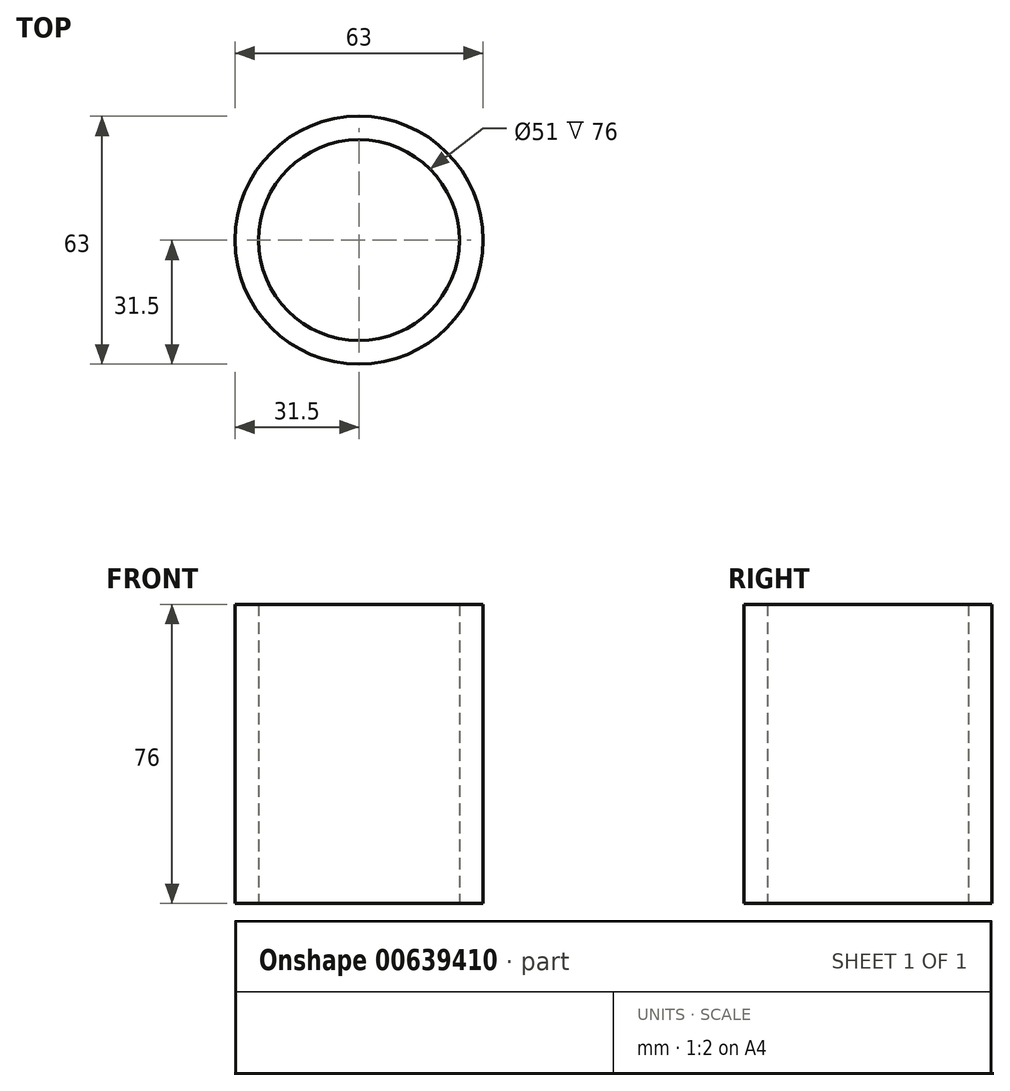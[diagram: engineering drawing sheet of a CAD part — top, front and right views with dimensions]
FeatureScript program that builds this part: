
annotation { "Feature Type Name" : "Feature", "Feature Type Description" : "" }
export const myFeature = defineFeature(function(context is Context, id is Id, definition is map)
    precondition{}
    {
        {
            var Q0;
            Q0=qCreatedBy(makeId("Top.planeOp"),FACE);
            var sketch = newSketch(context, id + "F0", { "sketchPlane" : qUnion([Q0])});
            skCircle(sketch, "E0", {"center": v(0, 0) * mm, "radius": 31.5 * mm});
            skCircle(sketch, "E1", {"center": v(0, 0) * mm, "radius": 25.5 * mm});
            skSolve(sketch);
        }
        {
            var Q0;
            Q0=makeQuery(id+"F0.imprint","IMPRINT",FACE,{"disambiguationData":[TD([[makeQuery(id+"F0.imprint","IMPRINT",EDGE,{"derivedFrom":sQuery(id+"F0.wireOp",EDGE,"E0")}),1.0]])]});
            extrude(context, id + "F1", {"entities" : qUnion([Q0]), "depth" : 76 * mm, "offsetDistance" : 25 * mm});
        }
    });
